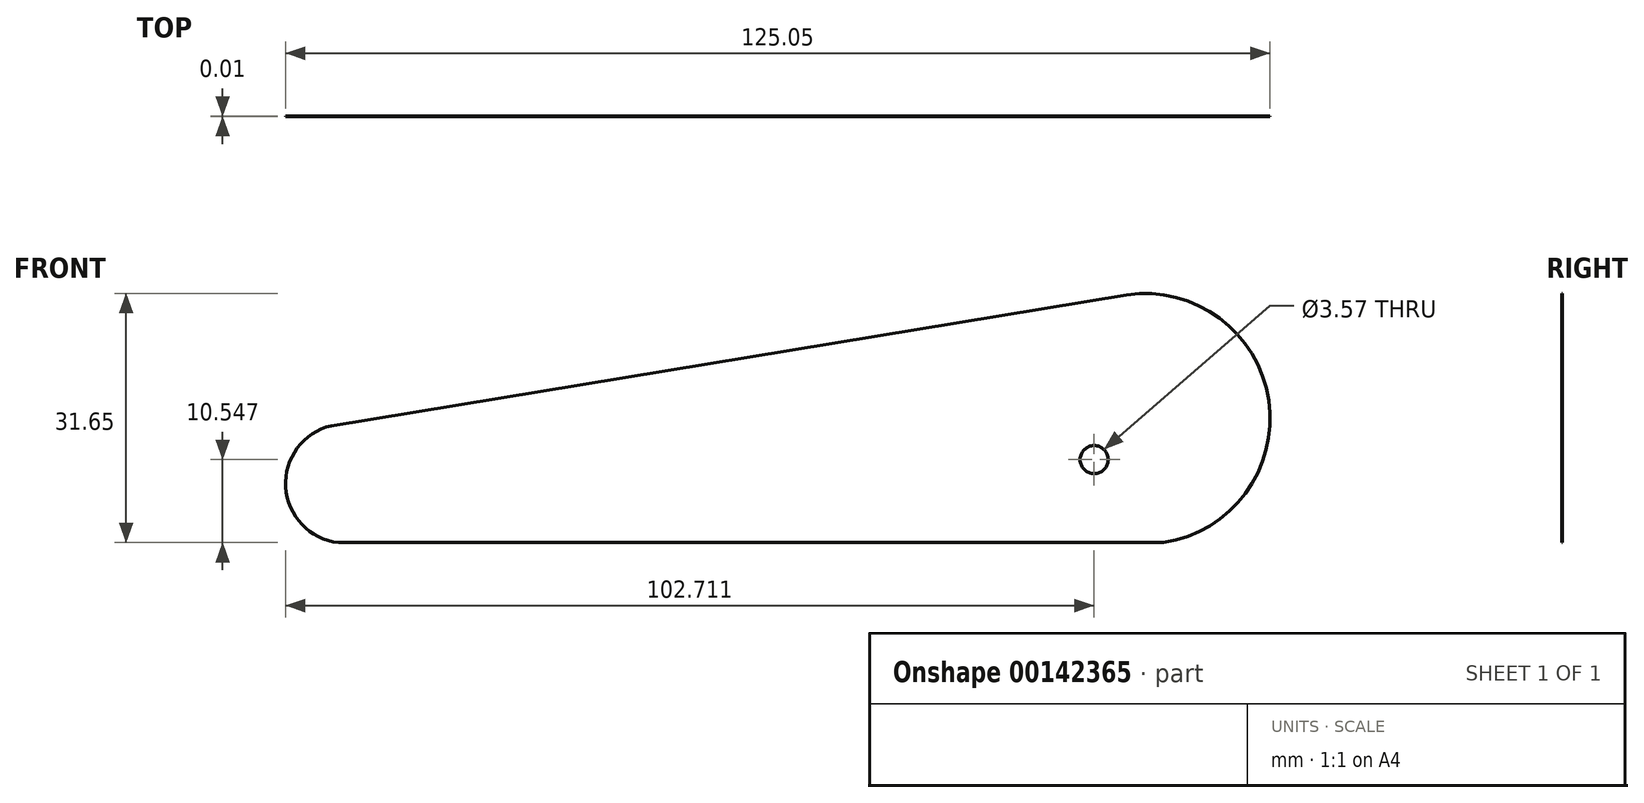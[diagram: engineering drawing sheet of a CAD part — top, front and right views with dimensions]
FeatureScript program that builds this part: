
annotation { "Feature Type Name" : "Feature", "Feature Type Description" : "" }
export const myFeature = defineFeature(function(context is Context, id is Id, definition is map)
    precondition{}
    {
        {
            var Q0;
            Q0=qCreatedBy(makeId("Front.planeOp"),FACE);
            var sketch = newSketch(context, id + "F0", { "sketchPlane" : qUnion([Q0])});
            skArc(sketch, "E0", {"start": v(-84.62, 7.42) * mm, "mid": v(-90.42, -0.38) * mm, "end": v(-83.73, -7.43) * mm});
            skArc(sketch, "E1", {"start": v(21.05, -7.43) * mm, "mid": v(34.45, 10.64) * mm, "end": v(16.39, 24.04) * mm});
            skLineSegment(sketch, "E2", {"start": v(-84.62, 7.42) * mm, "end": v(16.39, 24.04) * mm});
            skLineSegment(sketch, "E3", {"start": v(-83.73, -7.43) * mm, "end": v(21.05, -7.43) * mm});
            skSolve(sketch);
        }
        {
            var Q0;
            Q0 = qSketchRegion(id + "F0", true);
            extrude(context, id + "F1", {"entities" : qUnion([Q0]), "depth" : 11 / 812.8 * mm});
        }
        {
            var Q0;
            Q0=makeQuery(id+"F1.opExtrude","CAP_FACE",FACE,{"disambiguationData":[OSD([sQuery(id+"F0.wireOp",EDGE,"E0"),sQuery(id+"F0.wireOp",EDGE,"E1"),sQuery(id+"F0.wireOp",EDGE,"E2"),sQuery(id+"F0.wireOp",EDGE,"E3")])],"isStart":false});
            var sketch = newSketch(context, id + "F2", { "sketchPlane" : qUnion([Q0])});
            skCircle(sketch, "E4", {"center": v(12.28, 3.12) * mm, "radius": 1.79 * mm});
            skSolve(sketch);
        }
        {
            var Q0;
            Q0 = qSketchRegion(id + "F2", true);
            var Q1;
            Q1=makeQuery(id+"F1.opExtrude","CAP_FACE",FACE,{"disambiguationData":[OSD([sQuery(id+"F0.wireOp",EDGE,"E0"),sQuery(id+"F0.wireOp",EDGE,"E1"),sQuery(id+"F0.wireOp",EDGE,"E2"),sQuery(id+"F0.wireOp",EDGE,"E3")])],"isStart":true});
            extrude(context, id + "F3", {"entities" : qUnion([Q0]), "operationType" : NewBodyOperationType.REMOVE, "endBound" : BoundingType.UP_TO_SURFACE, "oppositeDirection" : true, "endBoundEntityFace" : qUnion([Q1]), "depth" : 25.4 * mm});
        }
    });
